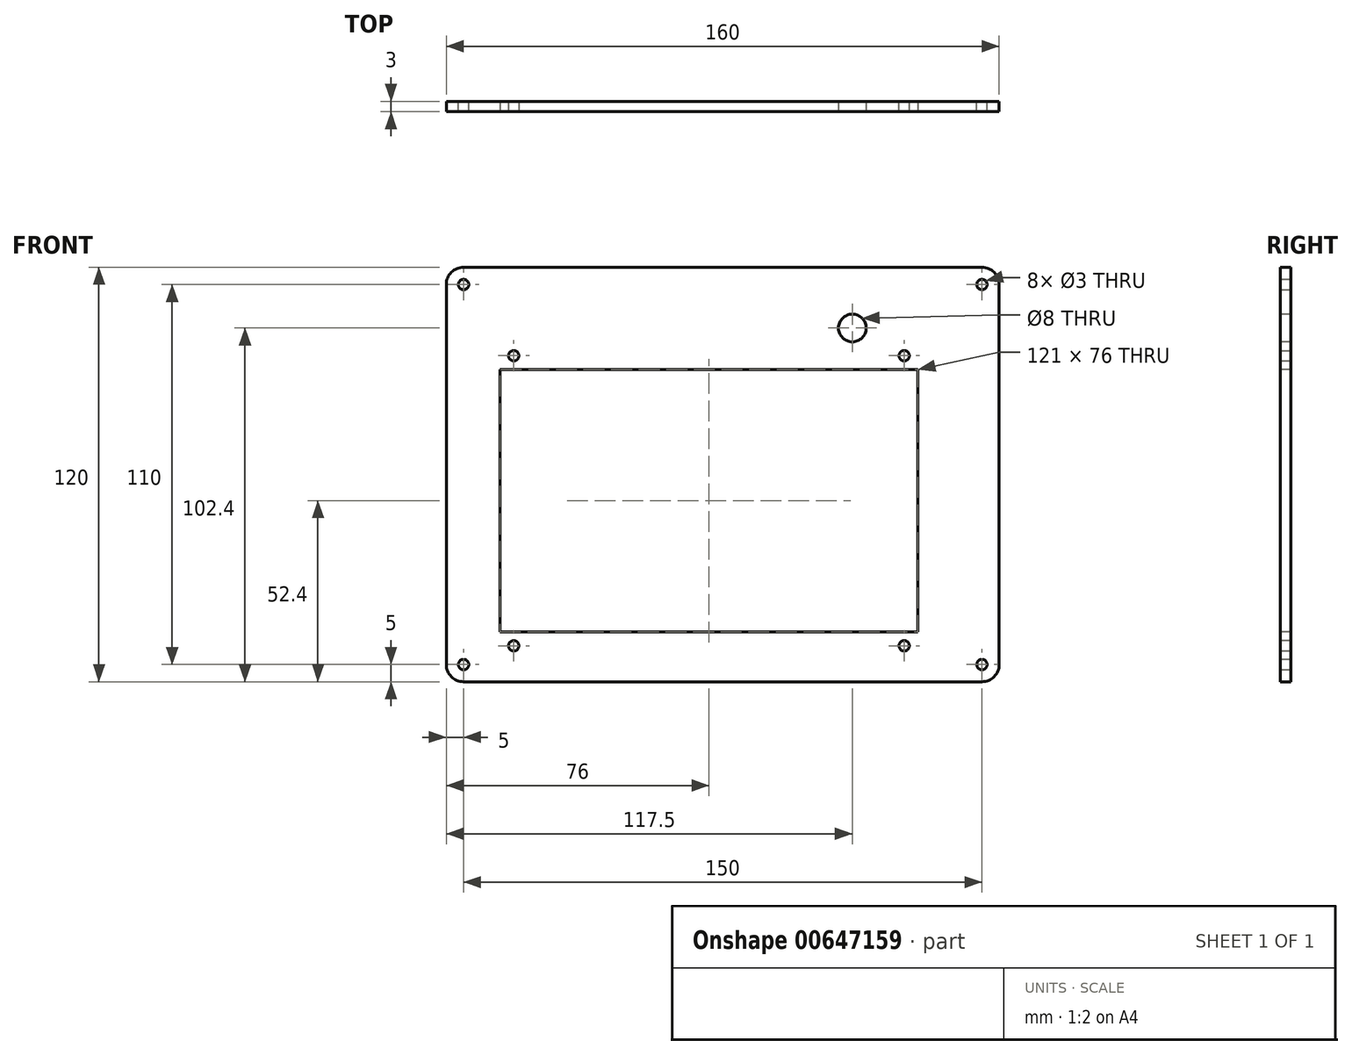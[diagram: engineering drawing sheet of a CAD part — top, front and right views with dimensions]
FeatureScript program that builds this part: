
annotation { "Feature Type Name" : "Feature", "Feature Type Description" : "" }
export const myFeature = defineFeature(function(context is Context, id is Id, definition is map)
    precondition{}
    {
        {
            var Q0;
            Q0=qCreatedBy(makeId("Front.planeOp"),FACE);
            var sketch = newSketch(context, id + "F0", { "sketchPlane" : qUnion([Q0])});
            skLineSegment(sketch, "E0.bottom", {"start": v(75, -60) * mm, "end": v(-75, -60) * mm});
            skLineSegment(sketch, "E0.top", {"start": v(75, 60) * mm, "end": v(-75, 60) * mm});
            skLineSegment(sketch, "E0.left", {"start": v(80, -55) * mm, "end": v(80, 55) * mm});
            skLineSegment(sketch, "E0.right", {"start": v(-80, -55) * mm, "end": v(-80, 55) * mm});
            skPoint(sketch, "E0.middle", {"position": v(0, 0) * mm});
            skPoint(sketch, "E1.visualSharp", {"position": v(-80, 60) * mm});
            skArc(sketch, "E1.filletArc", {"start": v(-75, 60) * mm, "mid": v(-78.54, 58.54) * mm, "end": v(-80, 55) * mm});
            skPoint(sketch, "E2.visualSharp", {"position": v(80, 60) * mm});
            skArc(sketch, "E2.filletArc", {"start": v(80, 55) * mm, "mid": v(78.54, 58.54) * mm, "end": v(75, 60) * mm});
            skPoint(sketch, "E3.visualSharp", {"position": v(80, -60) * mm});
            skArc(sketch, "E3.filletArc", {"start": v(75, -60) * mm, "mid": v(78.54, -58.54) * mm, "end": v(80, -55) * mm});
            skPoint(sketch, "E4.visualSharp", {"position": v(-80, -60) * mm});
            skArc(sketch, "E4.filletArc", {"start": v(-80, -55) * mm, "mid": v(-78.54, -58.54) * mm, "end": v(-75, -60) * mm});
            skSolve(sketch);
        }
        {
            var Q0;
            Q0=makeQuery(id+"F0.imprint","IMPRINT",FACE,{"disambiguationData":[TD([[makeQuery(id+"F0.imprint","IMPRINT",EDGE,{"derivedFrom":sQuery(id+"F0.wireOp",EDGE,"E0.bottom")}),-1.0]])]});
            extrude(context, id + "F1", {"entities" : qUnion([Q0]), "depth" : 3 * mm, "offsetDistance" : 25 * mm});
        }
        {
            var Q0;
            Q0=qCreatedBy(makeId("Front.planeOp"),FACE);
            var sketch = newSketch(context, id + "F2", { "sketchPlane" : qUnion([Q0])});
            skCircle(sketch, "E5", {"center": v(-75, 55) * mm, "radius": 1.5 * mm});
            skCircle(sketch, "E6", {"center": v(75, 55) * mm, "radius": 1.5 * mm});
            skCircle(sketch, "E7", {"center": v(75, -55) * mm, "radius": 1.5 * mm});
            skCircle(sketch, "E8", {"center": v(-75, -55) * mm, "radius": 1.5 * mm});
            skSolve(sketch);
        }
        {
            var Q0;
            Q0=qSketchRegion(id+"F2",true);
            extrude(context, id + "F3", {"entities" : qUnion([Q0]), "operationType" : NewBodyOperationType.REMOVE, "depth" : 25 * mm, "offsetDistance" : 25 * mm});
        }
        {
            var Q0;
            Q0=qCreatedBy(makeId("Front.planeOp"),FACE);
            var sketch = newSketch(context, id + "F4", { "sketchPlane" : qUnion([Q0])});
            skPoint(sketch, "E9.start.orphan", {"position": v(0, -27.1) * mm});
            skCircle(sketch, "E10", {"center": v(52.5, 34.4) * mm, "radius": 1.5 * mm});
            skSolve(sketch);
        }
        {
            var Q0;
            Q0=makeQuery(id+"F4.imprint","IMPRINT",FACE,{"disambiguationData":[TD([[makeQuery(id+"F4.imprint","IMPRINT",EDGE,{"derivedFrom":sQuery(id+"F4.wireOp",EDGE,"3Q8pNaT9-MZu4-fZL0-JBpA-oB1KTClbxi4n")}),1.0]])]});
            var Q1;
            Q1=makeQuery(id+"F4.imprint","IMPRINT",FACE,{"disambiguationData":[TD([[makeQuery(id+"F4.imprint","IMPRINT",EDGE,{"derivedFrom":sQuery(id+"F4.wireOp",EDGE,"E10")}),1.0]])]});
            var Q2;
            Q2=makeQuery(id+"F4.imprint","IMPRINT",FACE,{"disambiguationData":[TD([[makeQuery(id+"F4.imprint","IMPRINT",EDGE,{"derivedFrom":sQuery(id+"F4.wireOp",EDGE,"r2QVgMR1-3B4m-qnwO-mz9k-peFpHc5iAmY2")}),1.0]])]});
            var Q3;
            Q3=makeQuery(id+"F4.imprint","IMPRINT",FACE,{"disambiguationData":[TD([[makeQuery(id+"F4.imprint","IMPRINT",EDGE,{"derivedFrom":sQuery(id+"F4.wireOp",EDGE,"o2jHBMil-3RIS-sA2l-7ex4-zNIZPRWduCML")}),1.0]])]});
            extrude(context, id + "F5", {"entities" : qUnion([Q0, Q1, Q2, Q3]), "operationType" : NewBodyOperationType.REMOVE, "depth" : 25 * mm, "offsetDistance" : 25 * mm});
        }
        {
            var Q0;
            Q0=makeQuery(id+"F1.opExtrude","CAP_FACE",FACE,{"disambiguationData":[OSD([sQuery(id+"F0.wireOp",EDGE,"E0.bottom"),sQuery(id+"F0.wireOp",EDGE,"E0.top"),sQuery(id+"F0.wireOp",EDGE,"E0.left"),sQuery(id+"F0.wireOp",EDGE,"E0.right"),sQuery(id+"F0.wireOp",EDGE,"E1.filletArc"),sQuery(id+"F0.wireOp",EDGE,"E2.filletArc"),sQuery(id+"F0.wireOp",EDGE,"E3.filletArc"),sQuery(id+"F0.wireOp",EDGE,"E4.filletArc")])],"isStart":false});
            var sketch = newSketch(context, id + "F6", { "sketchPlane" : qUnion([Q0])});
            skLineSegment(sketch, "E11", {"start": v(-64.5, 30.4) * mm, "end": v(56.5, 30.4) * mm});
            skCircle(sketch, "E12.0", {"center": v(52.5, 34.4) * mm, "radius": 1.5 * mm});
            skCircle(sketch, "E13", {"center": v(-60.5, 34.4) * mm, "radius": 1.5 * mm});
            skCircle(sketch, "E14", {"center": v(-60.5, -49.6) * mm, "radius": 1.5 * mm});
            skCircle(sketch, "E15", {"center": v(52.5, -49.6) * mm, "radius": 1.5 * mm});
            skLineSegment(sketch, "E16", {"start": v(-64.5, -45.6) * mm, "end": v(56.5, -45.6) * mm});
            skLineSegment(sketch, "E17", {"start": v(-64.5, 30.4) * mm, "end": v(-64.5, -45.6) * mm});
            skLineSegment(sketch, "E18", {"start": v(56.5, 30.4) * mm, "end": v(56.5, -45.6) * mm});
            skSolve(sketch);
        }
        {
            var Q0;
            Q0 = qSketchRegion(id + "F6", true);
            extrude(context, id + "F7", {"entities" : qUnion([Q0]), "operationType" : NewBodyOperationType.REMOVE, "oppositeDirection" : true, "depth" : 3 * mm, "offsetDistance" : 25 * mm});
        }
        {
            var Q0;
            Q0=makeQuery(id+"F1.opExtrude","CAP_FACE",FACE,{"disambiguationData":[OSD([sQuery(id+"F0.wireOp",EDGE,"E0.bottom"),sQuery(id+"F0.wireOp",EDGE,"E0.top"),sQuery(id+"F0.wireOp",EDGE,"E0.left"),sQuery(id+"F0.wireOp",EDGE,"E0.right"),sQuery(id+"F0.wireOp",EDGE,"E1.filletArc"),sQuery(id+"F0.wireOp",EDGE,"E2.filletArc"),sQuery(id+"F0.wireOp",EDGE,"E3.filletArc"),sQuery(id+"F0.wireOp",EDGE,"E4.filletArc")])],"isStart":false});
            var sketch = newSketch(context, id + "F8", { "sketchPlane" : qUnion([Q0])});
            skCircle(sketch, "E19", {"center": v(37.5, 42.4) * mm, "radius": 4 * mm});
            skPoint(sketch, "E20.0.center.orphan", {"position": v(52.5, 34.4) * mm});
            skSolve(sketch);
        }
        {
            var Q0;
            Q0=makeQuery(id+"F8.imprint","IMPRINT",FACE,{"disambiguationData":[TD([[makeQuery(id+"F8.imprint","IMPRINT",EDGE,{"derivedFrom":sQuery(id+"F8.wireOp",EDGE,"E19")}),1.0]])]});
            extrude(context, id + "F9", {"entities" : qUnion([Q0]), "operationType" : NewBodyOperationType.REMOVE, "oppositeDirection" : true, "depth" : 3 * mm, "offsetDistance" : 25 * mm});
        }
    });
